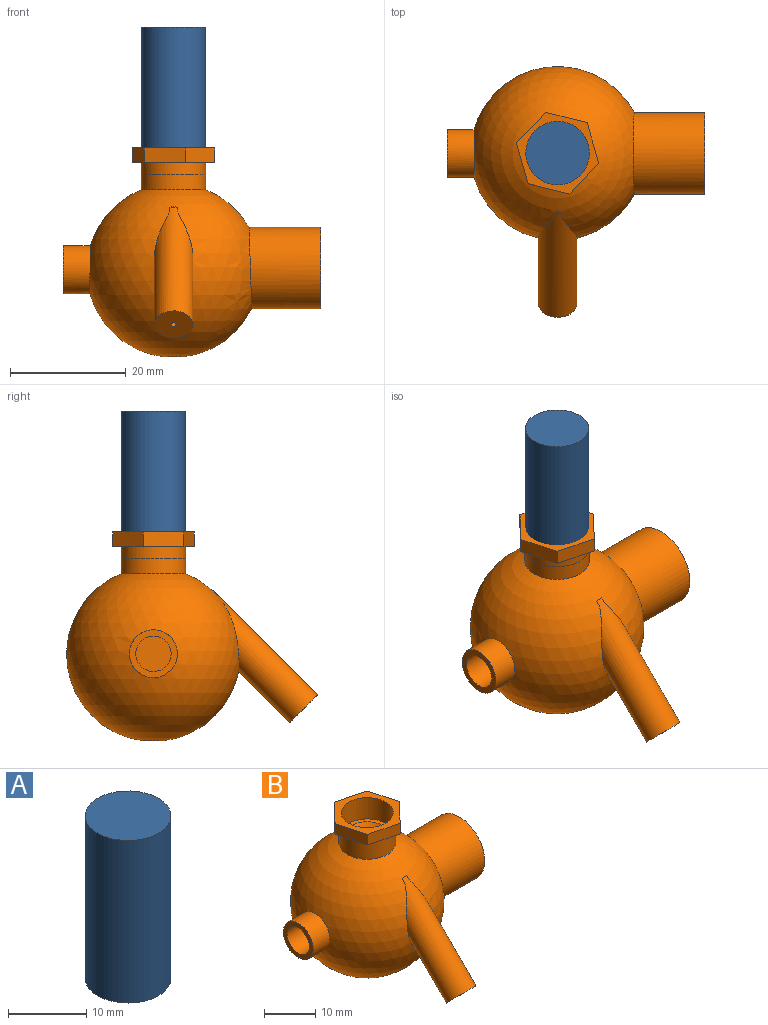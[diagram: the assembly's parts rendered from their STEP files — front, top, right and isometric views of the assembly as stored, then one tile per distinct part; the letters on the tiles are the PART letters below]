
ASSEMBLY  parts=2 mates=1
PART A: 3 faces, bbox 11x11x25.4 mm
  f0: cylinder r=5.48mm len=25.4mm, axis (0,0,-1), area 874.9mm2, adj f1,f2
  f1: plane 10.96x10.96mm, normal (0,0,1), area 94.4mm2, adj f0
  f2: plane 10.96x10.96mm, normal (0,0,-1), area 94.4mm2, adj f0
PART B: 27 faces, bbox 44.5x43.3x36.1 mm
  f0: cone r=1.93mm half-angle=41deg, axis (0,0,1), area 63.1mm2, adj f16,f18,f22
  f1: plane 7.05x2.54mm, normal (0.96,0.28,0), area 18.6mm2, adj f2,f6,f7,f8
  f2: plane 7.11x2.54mm, normal (0.24,0.97,0), area 18.6mm2, adj f1,f3,f7,f8
  f3: plane 5.27x5.1mm, normal (-0.72,0.7,0), area 18.6mm2, adj f2,f4,f7,f8
  f4: plane 7.05x2.54mm, normal (-0.96,-0.28,0), area 18.6mm2, adj f3,f5,f7,f8
  f5: plane 7.11x2.54mm, normal (-0.24,-0.97,0), area 18.6mm2, adj f4,f6,f7,f8
  f6: plane 5.27x5.1mm, normal (0.72,-0.7,0), area 18.6mm2, adj f1,f5,f7,f8
  f7: plane 14.23x14.1mm, normal (0,0,1), area 58.6mm2, adj f1,f2,f3,f4,f5,f6,f17
  f8: plane 14.23x14.1mm, normal (0,0,-1), area 42.8mm2, adj f1,f2,f3,f4,f5,f6,f9
  f9: cylinder r=5.55mm len=11.11mm, axis (0,0,1), area 162.9mm2, adj f8,f10
  f10: sphere r=15.01mm, area 2429.9mm2, adj f9,f11,f15,f19,f20,f24
  f11: cylinder r=7.03mm len=14.06mm, axis (1,0,0), area 536.5mm2, adj f10,f12
  f12: plane 14.06x14.06mm, normal (1,0,0), area 54.5mm2, adj f11,f13
  f13: cylinder r=5.66mm len=25.4mm, axis (1,0,0), area 892.1mm2, adj f12,f14,f15,f16
  f14: sphere r=5.66mm, area 189.5mm2, adj f13,f15,f16
  f15: cylinder r=1.93mm len=9.99mm, axis (0,0,1), area 120.1mm2, adj f10,f13,f14
  f16: cylinder r=1.93mm len=7.79mm, axis (0,0,1), area 93.5mm2, adj f0,f13,f14
  f17: cylinder r=5.08mm len=10.16mm, axis (0,0,1), area 162.1mm2, adj f7,f18
  f18: plane 10.16x10.16mm, normal (0,0,1), area 27.6mm2, adj f0,f17
  f19: cylinder r=3.34mm len=22.69mm, axis (0,-0.71,-0.71), area 360.1mm2, adj f10,f20,f21
  f20: plane 1.38x0.08mm, normal (0,0.71,0.71), area 0mm2, adj f10,f19
  f21: plane 6.68x4.73mm, normal (0,-0.71,-0.71), area 34.5mm2, adj f19,f22
  f22: cylinder r=0.45mm len=24.1mm, axis (0,-0.71,-0.71), area 93.9mm2, adj f0,f21
  f23: plane 8.26x8.26mm, normal (-1,0,0), area 24.4mm2, adj f24,f25
  f24: cylinder r=4.13mm len=8.26mm, axis (-1,0,0), area 119.5mm2, adj f10,f23
  f25: cylinder r=3.05mm len=8.89mm, axis (-1,0,0), area 170.2mm2, adj f23,f26
  f26: plane 6.1x6.1mm, normal (-1,0,0), area 29.2mm2, adj f25
PLACE A rot(axis=(0,0,-1),90deg) t=(2.28,7.33,27.11)mm
PLACE B rot(axis=(0.25,0.64,0.72),0deg) t=(2.28,7.33,29.14)mm fixed
MATE fastened A.f0 <-> B.f0  axis (0,0,-1) through (2.28,7.33,27.11)mm
